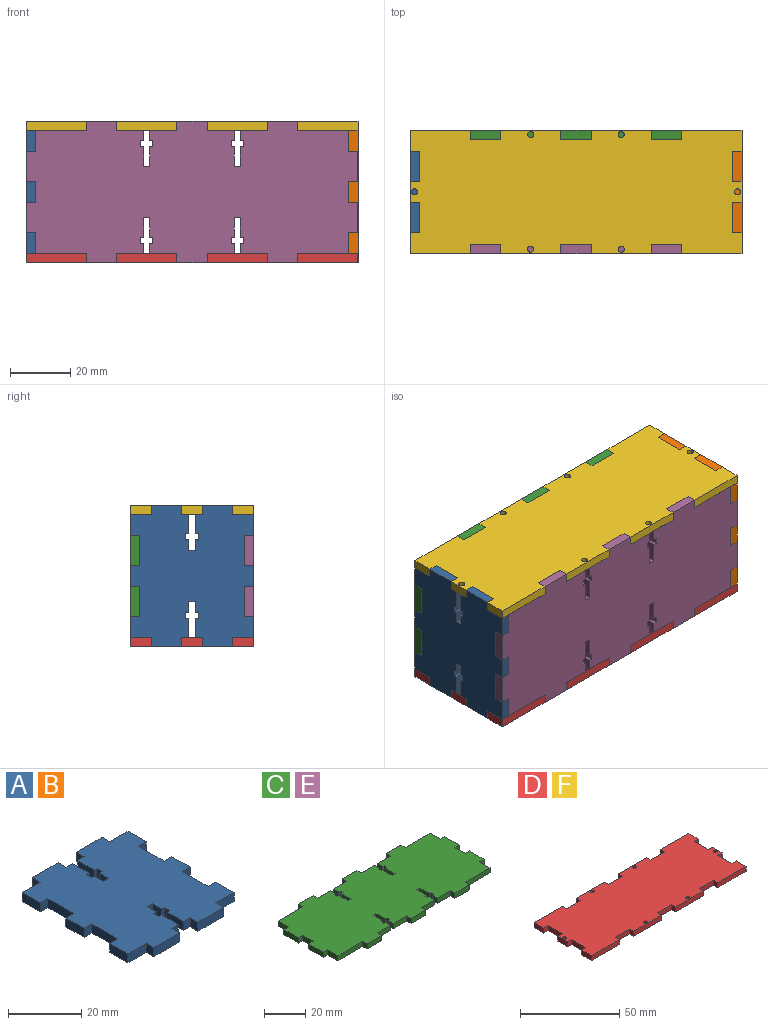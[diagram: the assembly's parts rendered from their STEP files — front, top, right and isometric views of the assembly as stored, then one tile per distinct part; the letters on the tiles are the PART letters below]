
ASSEMBLY  parts=6 mates=5
PART A: 62 faces, bbox 41x47x3 mm
  f0: plane 3x3mm, normal (1,0,0), area 9mm2, adj f1,f59,f60,f61
  f1: plane 7x3mm, normal (0,-1,0), area 21mm2, adj f0,f2,f60,f61
  f2: plane 7x3mm, normal (1,0,0), area 21mm2, adj f1,f3,f60,f61
  f3: plane 3x3mm, normal (0,1,0), area 9mm2, adj f2,f4,f60,f61
  f4: plane 10x3mm, normal (1,0,0), area 30mm2, adj f3,f5,f60,f61
  f5: plane 3x3mm, normal (0,-1,0), area 9mm2, adj f4,f6,f60,f61
  f6: plane 7x3mm, normal (1,0,0), area 21mm2, adj f5,f7,f60,f61
  f7: plane 3x3mm, normal (0,1,0), area 9mm2, adj f6,f8,f60,f61
  f8: plane 10x3mm, normal (1,0,0), area 30mm2, adj f7,f9,f60,f61
  f9: plane 3x3mm, normal (0,-1,0), area 9mm2, adj f8,f10,f60,f61
  f10: plane 7x3mm, normal (1,0,0), area 21mm2, adj f9,f11,f60,f61
  f11: plane 7x3mm, normal (0,1,0), area 21mm2, adj f10,f12,f60,f61
  f12: plane 3x3mm, normal (1,0,0), area 9mm2, adj f11,f13,f60,f61
  f13: plane 10x3mm, normal (0,1,0), area 30mm2, adj f12,f14,f60,f61
  f14: plane 3x3mm, normal (-1,0,0), area 9mm2, adj f13,f15,f60,f61
  f15: plane 3x2.5mm, normal (0,1,0), area 7.5mm2, adj f14,f16,f60,f61
  f16: plane 6.5x3mm, normal (-1,0,0), area 19.5mm2, adj f15,f17,f60,f61
  f17: plane 3x1mm, normal (0,-1,0), area 3mm2, adj f16,f18,f60,f61
  f18: plane 3x2mm, normal (-1,0,0), area 6mm2, adj f17,f19,f60,f61
  f19: plane 3x1mm, normal (0,1,0), area 3mm2, adj f18,f20,f60,f61
  f20: plane 3.5x3mm, normal (-1,0,0), area 10.5mm2, adj f19,f21,f60,f61
  f21: plane 3x2mm, normal (0,1,0), area 6mm2, adj f20,f22,f60,f61
  f22: plane 3.5x3mm, normal (1,0,0), area 10.5mm2, adj f21,f23,f60,f61
  f23: plane 3x1mm, normal (0,1,0), area 3mm2, adj f22,f24,f60,f61
  f24: plane 3x2mm, normal (1,0,0), area 6mm2, adj f23,f25,f60,f61
  f25: plane 3x1mm, normal (0,-1,0), area 3mm2, adj f24,f26,f60,f61
  f26: plane 6.5x3mm, normal (1,0,0), area 19.5mm2, adj f25,f27,f60,f61
  f27: plane 3x2.5mm, normal (0,1,0), area 7.5mm2, adj f26,f28,f60,f61
  f28: plane 3x3mm, normal (1,0,0), area 9mm2, adj f27,f29,f60,f61
  f29: plane 10x3mm, normal (0,1,0), area 30mm2, adj f28,f30,f60,f61
  f30: plane 3x3mm, normal (-1,0,0), area 9mm2, adj f29,f31,f60,f61
  f31: plane 7x3mm, normal (0,1,0), area 21mm2, adj f30,f32,f60,f61
  f32: plane 7x3mm, normal (-1,0,0), area 21mm2, adj f31,f33,f60,f61
  f33: plane 3x3mm, normal (0,-1,0), area 9mm2, adj f32,f34,f60,f61
  f34: plane 10x3mm, normal (-1,0,0), area 30mm2, adj f33,f35,f60,f61
  f35: plane 3x3mm, normal (0,1,0), area 9mm2, adj f34,f36,f60,f61
  f36: plane 7x3mm, normal (-1,0,0), area 21mm2, adj f35,f37,f60,f61
  f37: plane 3x3mm, normal (0,-1,0), area 9mm2, adj f36,f38,f60,f61
  f38: plane 10x3mm, normal (-1,0,0), area 30mm2, adj f37,f39,f60,f61
  f39: plane 3x3mm, normal (0,1,0), area 9mm2, adj f38,f40,f60,f61
  f40: plane 7x3mm, normal (-1,0,0), area 21mm2, adj f39,f41,f60,f61
  f41: plane 7x3mm, normal (0,-1,0), area 21mm2, adj f40,f42,f60,f61
  f42: plane 3x3mm, normal (-1,0,0), area 9mm2, adj f41,f43,f60,f61
  f43: plane 10x3mm, normal (0,-1,0), area 30mm2, adj f42,f44,f60,f61
  f44: plane 3x3mm, normal (1,0,0), area 9mm2, adj f43,f45,f60,f61
  f45: plane 3x2.5mm, normal (0,-1,0), area 7.5mm2, adj f44,f46,f60,f61
  f46: plane 6.5x3mm, normal (1,0,0), area 19.5mm2, adj f45,f47,f60,f61
  f47: plane 3x1mm, normal (0,1,0), area 3mm2, adj f46,f48,f60,f61
  f48: plane 3x2mm, normal (1,0,0), area 6mm2, adj f47,f49,f60,f61
  f49: plane 3x1mm, normal (0,-1,0), area 3mm2, adj f48,f50,f60,f61
  f50: plane 3.5x3mm, normal (1,0,0), area 10.5mm2, adj f49,f51,f60,f61
  f51: plane 3x2mm, normal (0,-1,0), area 6mm2, adj f50,f52,f60,f61
  f52: plane 3.5x3mm, normal (-1,0,0), area 10.5mm2, adj f51,f53,f60,f61
  f53: plane 3x1mm, normal (0,-1,0), area 3mm2, adj f52,f54,f60,f61
  f54: plane 3x2mm, normal (-1,0,0), area 6mm2, adj f53,f55,f60,f61
  f55: plane 3x1mm, normal (0,1,0), area 3mm2, adj f54,f56,f60,f61
  f56: plane 6.5x3mm, normal (-1,0,0), area 19.5mm2, adj f55,f57,f60,f61
  f57: plane 3x2.5mm, normal (0,-1,0), area 7.5mm2, adj f56,f58,f60,f61
  f58: plane 3x3mm, normal (-1,0,0), area 9mm2, adj f57,f59,f60,f61
  f59: plane 10x3mm, normal (0,-1,0), area 30mm2, adj f0,f58,f60,f61
  f60: plane 47x41mm, normal (0,0,1), area 1625mm2, adj f0,f1,f2,f3,f4,f5,f6,f7
  f61: plane 47x41mm, normal (0,0,-1), area 1625mm2, adj f0,f1,f2,f3,f4,f5,f6,f7
PART B: same geometry as A
PART C: 94 faces, bbox 110x47x3 mm
  f0: plane 3x3mm, normal (0,1,0), area 9mm2, adj f1,f91,f92,f93
  f1: plane 7x3mm, normal (1,0,0), area 21mm2, adj f0,f2,f92,f93
  f2: plane 17x3mm, normal (0,1,0), area 51mm2, adj f1,f3,f92,f93
  f3: plane 3x3mm, normal (1,0,0), area 9mm2, adj f2,f4,f92,f93
  f4: plane 10x3mm, normal (0,1,0), area 30mm2, adj f3,f5,f92,f93
  f5: plane 3x3mm, normal (-1,0,0), area 9mm2, adj f4,f6,f92,f93
  f6: plane 8.97x3mm, normal (0,1,0), area 26.9mm2, adj f5,f7,f92,f93
  f7: plane 3.5x3mm, normal (-1,0,0), area 10.5mm2, adj f6,f8,f92,f93
  f8: plane 3x1mm, normal (0,-1,0), area 3mm2, adj f7,f9,f92,f93
  f9: plane 3x2mm, normal (-1,0,0), area 6mm2, adj f8,f10,f92,f93
  f10: plane 3x1mm, normal (0,1,0), area 3mm2, adj f9,f11,f92,f93
  f11: plane 6.5x3mm, normal (-1,0,0), area 19.5mm2, adj f10,f12,f92,f93
  f12: plane 3x2mm, normal (0,1,0), area 6mm2, adj f11,f13,f92,f93
  f13: plane 6.5x3mm, normal (1,0,0), area 19.5mm2, adj f12,f14,f92,f93
  f14: plane 3x1mm, normal (0,1,0), area 3mm2, adj f13,f15,f92,f93
  f15: plane 3x2mm, normal (1,0,0), area 6mm2, adj f14,f16,f92,f93
  f16: plane 3x1mm, normal (0,-1,0), area 3mm2, adj f15,f17,f92,f93
  f17: plane 3.5x3mm, normal (1,0,0), area 10.5mm2, adj f16,f18,f92,f93
  f18: plane 9.03x3mm, normal (0,1,0), area 27.1mm2, adj f17,f19,f92,f93
  f19: plane 3x3mm, normal (1,0,0), area 9mm2, adj f18,f20,f92,f93
  f20: plane 10x3mm, normal (0,1,0), area 30mm2, adj f19,f21,f92,f93
  f21: plane 3x3mm, normal (-1,0,0), area 9mm2, adj f20,f22,f92,f93
  f22: plane 9.03x3mm, normal (0,1,0), area 27.1mm2, adj f21,f23,f92,f93
  f23: plane 3.5x3mm, normal (-1,0,0), area 10.5mm2, adj f22,f24,f92,f93
  f24: plane 3x1mm, normal (0,-1,0), area 3mm2, adj f23,f25,f92,f93
  f25: plane 3x2mm, normal (-1,0,0), area 6mm2, adj f24,f26,f92,f93
  f26: plane 3x1mm, normal (0,1,0), area 3mm2, adj f25,f27,f92,f93
  f27: plane 6.5x3mm, normal (-1,0,0), area 19.5mm2, adj f26,f28,f92,f93
  f28: plane 3x2mm, normal (0,1,0), area 6mm2, adj f27,f29,f92,f93
  f29: plane 6.5x3mm, normal (1,0,0), area 19.5mm2, adj f28,f30,f92,f93
  f30: plane 3x1mm, normal (0,1,0), area 3mm2, adj f29,f31,f92,f93
  f31: plane 3x2mm, normal (1,0,0), area 6mm2, adj f30,f32,f92,f93
  f32: plane 3x1mm, normal (0,-1,0), area 3mm2, adj f31,f33,f92,f93
  f33: plane 3.5x3mm, normal (1,0,0), area 10.5mm2, adj f32,f34,f92,f93
  f34: plane 8.97x3mm, normal (0,1,0), area 26.9mm2, adj f33,f35,f92,f93
  f35: plane 3x3mm, normal (1,0,0), area 9mm2, adj f34,f36,f92,f93
  f36: plane 10x3mm, normal (0,1,0), area 30mm2, adj f35,f37,f92,f93
  f37: plane 3x3mm, normal (-1,0,0), area 9mm2, adj f36,f38,f92,f93
  f38: plane 17x3mm, normal (0,1,0), area 51mm2, adj f37,f39,f92,f93
  f39: plane 7x3mm, normal (-1,0,0), area 21mm2, adj f38,f40,f92,f93
  f40: plane 3x3mm, normal (0,1,0), area 9mm2, adj f39,f41,f92,f93
  f41: plane 10x3mm, normal (-1,0,0), area 30mm2, adj f40,f42,f92,f93
  f42: plane 3x3mm, normal (0,-1,0), area 9mm2, adj f41,f43,f92,f93
  f43: plane 7x3mm, normal (-1,0,0), area 21mm2, adj f42,f44,f92,f93
  f44: plane 3x3mm, normal (0,1,0), area 9mm2, adj f43,f45,f92,f93
  f45: plane 10x3mm, normal (-1,0,0), area 30mm2, adj f44,f46,f92,f93
  f46: plane 3x3mm, normal (0,-1,0), area 9mm2, adj f45,f47,f92,f93
  f47: plane 7x3mm, normal (-1,0,0), area 21mm2, adj f46,f48,f92,f93
  f48: plane 17x3mm, normal (0,-1,0), area 51mm2, adj f47,f49,f92,f93
  f49: plane 3x3mm, normal (-1,0,0), area 9mm2, adj f48,f50,f92,f93
  f50: plane 10x3mm, normal (0,-1,0), area 30mm2, adj f49,f51,f92,f93
  f51: plane 3x3mm, normal (1,0,0), area 9mm2, adj f50,f52,f92,f93
  f52: plane 8.97x3mm, normal (0,-1,0), area 26.9mm2, adj f51,f53,f92,f93
  f53: plane 3.5x3mm, normal (1,0,0), area 10.5mm2, adj f52,f54,f92,f93
  f54: plane 3x1mm, normal (0,1,0), area 3mm2, adj f53,f55,f92,f93
  f55: plane 3x2mm, normal (1,0,0), area 6mm2, adj f54,f56,f92,f93
  f56: plane 3x1mm, normal (0,-1,0), area 3mm2, adj f55,f57,f92,f93
  f57: plane 6.5x3mm, normal (1,0,0), area 19.5mm2, adj f56,f58,f92,f93
  f58: plane 3x2mm, normal (0,-1,0), area 6mm2, adj f57,f59,f92,f93
  f59: plane 6.5x3mm, normal (-1,0,0), area 19.5mm2, adj f58,f60,f92,f93
  f60: plane 3x1mm, normal (0,-1,0), area 3mm2, adj f59,f61,f92,f93
  f61: plane 3x2mm, normal (-1,0,0), area 6mm2, adj f60,f62,f92,f93
  f62: plane 3x1mm, normal (0,1,0), area 3mm2, adj f61,f63,f92,f93
  f63: plane 3.5x3mm, normal (-1,0,0), area 10.5mm2, adj f62,f64,f92,f93
  f64: plane 9.03x3mm, normal (0,-1,0), area 27.1mm2, adj f63,f65,f92,f93
  f65: plane 3x3mm, normal (-1,0,0), area 9mm2, adj f64,f66,f92,f93
  f66: plane 10x3mm, normal (0,-1,0), area 30mm2, adj f65,f67,f92,f93
  f67: plane 3x3mm, normal (1,0,0), area 9mm2, adj f66,f68,f92,f93
  f68: plane 9.03x3mm, normal (0,-1,0), area 27.1mm2, adj f67,f69,f92,f93
  f69: plane 3.5x3mm, normal (1,0,0), area 10.5mm2, adj f68,f70,f92,f93
  f70: plane 3x1mm, normal (0,1,0), area 3mm2, adj f69,f71,f92,f93
  f71: plane 3x2mm, normal (1,0,0), area 6mm2, adj f70,f72,f92,f93
  f72: plane 3x1mm, normal (0,-1,0), area 3mm2, adj f71,f73,f92,f93
  f73: plane 6.5x3mm, normal (1,0,0), area 19.5mm2, adj f72,f74,f92,f93
  f74: plane 3x2mm, normal (0,-1,0), area 6mm2, adj f73,f75,f92,f93
  f75: plane 6.5x3mm, normal (-1,0,0), area 19.5mm2, adj f74,f76,f92,f93
  f76: plane 3x1mm, normal (0,-1,0), area 3mm2, adj f75,f77,f92,f93
  f77: plane 3x2mm, normal (-1,0,0), area 6mm2, adj f76,f78,f92,f93
  f78: plane 3x1mm, normal (0,1,0), area 3mm2, adj f77,f79,f92,f93
  f79: plane 3.5x3mm, normal (-1,0,0), area 10.5mm2, adj f78,f80,f92,f93
  f80: plane 8.97x3mm, normal (0,-1,0), area 26.9mm2, adj f79,f81,f92,f93
  f81: plane 3x3mm, normal (-1,0,0), area 9mm2, adj f80,f82,f92,f93
  f82: plane 10x3mm, normal (0,-1,0), area 30mm2, adj f81,f83,f92,f93
  f83: plane 3x3mm, normal (1,0,0), area 9mm2, adj f82,f84,f92,f93
  f84: plane 17x3mm, normal (0,-1,0), area 51mm2, adj f83,f85,f92,f93
  f85: plane 7x3mm, normal (1,0,0), area 21mm2, adj f84,f86,f92,f93
  f86: plane 3x3mm, normal (0,-1,0), area 9mm2, adj f85,f87,f92,f93
  f87: plane 10x3mm, normal (1,0,0), area 30mm2, adj f86,f88,f92,f93
  f88: plane 3x3mm, normal (0,1,0), area 9mm2, adj f87,f89,f92,f93
  f89: plane 7x3mm, normal (1,0,0), area 21mm2, adj f88,f90,f92,f93
  f90: plane 3x3mm, normal (0,-1,0), area 9mm2, adj f89,f91,f92,f93
  f91: plane 10x3mm, normal (1,0,0), area 30mm2, adj f0,f90,f92,f93
  f92: plane 110x47mm, normal (0,0,1), area 4452mm2, adj f0,f1,f2,f3,f4,f5,f6,f7
  f93: plane 110x47mm, normal (0,0,-1), area 4452mm2, adj f0,f1,f2,f3,f4,f5,f6,f7
PART D: 52 faces, bbox 110x41x3 mm
  f0: plane 3x3mm, normal (0,1,0), area 9mm2, adj f1,f49,f50,f51
  f1: plane 10x3mm, normal (1,0,0), area 30mm2, adj f0,f2,f50,f51
  f2: plane 3x3mm, normal (0,-1,0), area 9mm2, adj f1,f3,f50,f51
  f3: plane 7x3mm, normal (1,0,0), area 21mm2, adj f2,f4,f50,f51
  f4: plane 3x3mm, normal (0,1,0), area 9mm2, adj f3,f5,f50,f51
  f5: plane 10x3mm, normal (1,0,0), area 30mm2, adj f4,f6,f50,f51
  f6: plane 3x3mm, normal (0,-1,0), area 9mm2, adj f5,f7,f50,f51
  f7: plane 7x3mm, normal (1,0,0), area 21mm2, adj f6,f8,f50,f51
  f8: plane 20x3mm, normal (0,1,0), area 60mm2, adj f7,f9,f50,f51
  f9: plane 3x3mm, normal (-1,0,0), area 9mm2, adj f8,f10,f50,f51
  f10: plane 10x3mm, normal (0,1,0), area 30mm2, adj f9,f11,f50,f51
  f11: plane 3x3mm, normal (1,0,0), area 9mm2, adj f10,f12,f50,f51
  f12: plane 20x3mm, normal (0,1,0), area 60mm2, adj f11,f13,f50,f51
  f13: plane 3x3mm, normal (-1,0,0), area 9mm2, adj f12,f14,f50,f51
  f14: plane 10x3mm, normal (0,1,0), area 30mm2, adj f13,f15,f50,f51
  f15: plane 3x3mm, normal (1,0,0), area 9mm2, adj f14,f16,f50,f51
  f16: plane 20x3mm, normal (0,1,0), area 60mm2, adj f15,f17,f50,f51
  f17: plane 3.01x3mm, normal (-1,0,0), area 9mm2, adj f16,f18,f50,f51
  f18: plane 10x3mm, normal (0,1,0), area 30mm2, adj f17,f19,f50,f51
  f19: plane 3.01x3mm, normal (1,0,0), area 9mm2, adj f18,f20,f50,f51
  f20: plane 20x3mm, normal (0,1,0), area 60mm2, adj f19,f21,f50,f51
  f21: plane 7x3mm, normal (-1,0,0), area 21mm2, adj f20,f22,f50,f51
  f22: plane 3x3mm, normal (0,-1,0), area 9mm2, adj f21,f23,f50,f51
  f23: plane 10x3mm, normal (-1,0,0), area 30mm2, adj f22,f24,f50,f51
  f24: plane 3x3mm, normal (0,1,0), area 9mm2, adj f23,f25,f50,f51
  f25: plane 7x3mm, normal (-1,0,0), area 21mm2, adj f24,f26,f50,f51
  f26: plane 3x3mm, normal (0,-1,0), area 9mm2, adj f25,f27,f50,f51
  f27: plane 10x3mm, normal (-1,0,0), area 30mm2, adj f26,f28,f50,f51
  f28: plane 3x3mm, normal (0,1,0), area 9mm2, adj f27,f29,f50,f51
  f29: plane 7x3mm, normal (-1,0,0), area 21mm2, adj f28,f30,f50,f51
  f30: plane 20x3mm, normal (0,-1,0), area 60mm2, adj f29,f31,f50,f51
  f31: plane 3x2.99mm, normal (1,0,0), area 9mm2, adj f30,f32,f50,f51
  f32: plane 10x3mm, normal (0,-1,0), area 30mm2, adj f31,f33,f50,f51
  f33: plane 3x2.99mm, normal (-1,0,0), area 9mm2, adj f32,f34,f50,f51
  f34: plane 20x3mm, normal (0,-1,0), area 60mm2, adj f33,f35,f50,f51
  f35: plane 3x3mm, normal (1,0,0), area 9mm2, adj f34,f36,f50,f51
  f36: plane 10x3mm, normal (0,-1,0), area 30mm2, adj f35,f37,f50,f51
  f37: plane 3x3mm, normal (-1,0,0), area 9mm2, adj f36,f38,f50,f51
  f38: plane 20x3mm, normal (0,-1,0), area 60mm2, adj f37,f39,f50,f51
  f39: plane 3x3mm, normal (1,0,0), area 9mm2, adj f38,f40,f50,f51
  f40: plane 10x3mm, normal (0,-1,0), area 30mm2, adj f39,f41,f50,f51
  f41: plane 3x3mm, normal (-1,0,0), area 9mm2, adj f40,f42,f50,f51
  f42: plane 20x3mm, normal (0,-1,0), area 60mm2, adj f41,f49,f50,f51
  f43: cylinder r=1mm len=3mm, axis (0,0,-1), area 18.8mm2, adj f50,f51
  f44: cylinder r=1mm len=3mm, axis (0,0,-1), area 18.8mm2, adj f50,f51
  f45: cylinder r=1mm len=3mm, axis (0,0,-1), area 18.8mm2, adj f50,f51
  f46: cylinder r=1mm len=3mm, axis (0,0,-1), area 18.8mm2, adj f50,f51
  f47: cylinder r=1mm len=3mm, axis (0,0,-1), area 18.8mm2, adj f50,f51
  f48: cylinder r=1mm len=3mm, axis (0,0,-1), area 18.8mm2, adj f50,f51
  f49: plane 7x3mm, normal (1,0,0), area 21mm2, adj f0,f42,f50,f51
  f50: plane 110x41mm, normal (0,0,1), area 4191.2mm2, adj f0,f1,f2,f3,f4,f5,f6,f7
  f51: plane 110x41mm, normal (0,0,-1), area 4191.2mm2, adj f0,f1,f2,f3,f4,f5,f6,f7
PART E: same geometry as C
PART F: same geometry as D
PLACE A rot(axis=(-0.58,0.58,-0.58),120deg) t=(-84.87,-40.56,14.89)mm
PLACE B rot(axis=(-0.58,-0.58,0.58),120deg) t=(25.13,45.14,14.89)mm
PLACE C rot(axis=(-1,0,0),90deg) t=(-36.68,19.79,0.4)mm
PLACE D rot(axis=(1,0,0),0deg) t=(-4.87,-4.66,-16.2)mm
PLACE E rot(axis=(1,0,0),90deg) t=(-36.68,-15.21,14.21)mm
PLACE F t=(-4.87,-4.66,27.8)mm
MATE fastened B.f60 <-> F.f5  axis (-1,0,0) through (22.13,10.79,30.8)mm
MATE fastened D.f50 <-> A.f11  axis (0,0,1) through (-84.87,-14.71,-13.2)mm
MATE fastened A.f60 <-> F.f27  axis (1,0,0) through (-81.87,-6.21,30.8)mm
MATE fastened C.f93 <-> B.f4  axis (0,-1,0) through (25.13,19.79,15.8)mm
MATE fastened E.f93 <-> F.f40  axis (0,1,0) through (0.13,-15.21,30.8)mm
